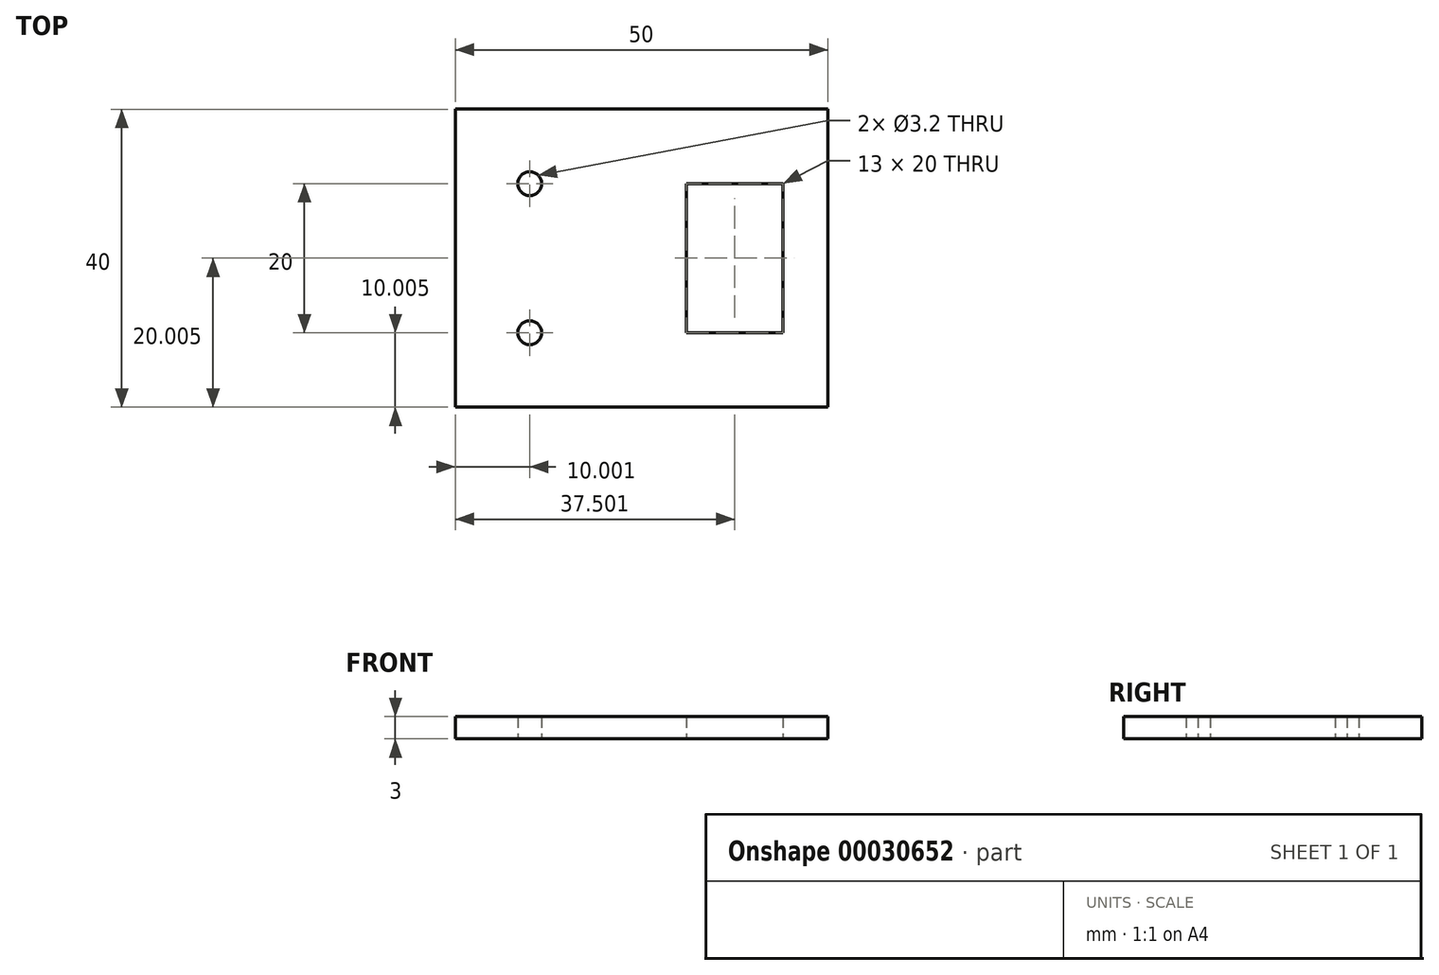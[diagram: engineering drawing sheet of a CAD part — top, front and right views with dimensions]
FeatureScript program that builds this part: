
annotation { "Feature Type Name" : "Feature", "Feature Type Description" : "" }
export const myFeature = defineFeature(function(context is Context, id is Id, definition is map)
    precondition{}
    {
        {
            var Q0;
            Q0=qCreatedBy(makeId("Top.planeOp"),FACE);
            var sketch = newSketch(context, id + "F0", { "sketchPlane" : qUnion([Q0])});
            skLineSegment(sketch, "E0.bottom", {"start": v(-26.16, 28.08) * mm, "end": v(23.84, 28.08) * mm});
            skLineSegment(sketch, "E0.top", {"start": v(-26.16, -11.92) * mm, "end": v(23.84, -11.92) * mm});
            skLineSegment(sketch, "E0.left", {"start": v(-26.16, 28.08) * mm, "end": v(-26.16, -11.92) * mm});
            skLineSegment(sketch, "E0.right", {"start": v(23.84, 28.08) * mm, "end": v(23.84, -11.92) * mm});
            skLineSegment(sketch, "E1.bottom", {"start": v(4.84, 18.08) * mm, "end": v(17.84, 18.08) * mm});
            skLineSegment(sketch, "E1.top", {"start": v(4.84, -1.92) * mm, "end": v(17.84, -1.92) * mm});
            skLineSegment(sketch, "E1.left", {"start": v(4.84, 18.08) * mm, "end": v(4.84, -1.92) * mm});
            skLineSegment(sketch, "E1.right", {"start": v(17.84, 18.08) * mm, "end": v(17.84, -1.92) * mm});
            skLineSegment(sketch, "E2", {"start": v(-26.16, 28.08) * mm, "end": v(-26.16, 18.08) * mm});
            skLineSegment(sketch, "E3", {"start": v(-26.16, 28.08) * mm, "end": v(-16.16, 28.08) * mm});
            skPoint(sketch, "E4", {"position": v(-16.16, 18.08) * mm});
            skCircle(sketch, "E5", {"center": v(-16.16, 18.08) * mm, "radius": 1.6 * mm});
            skCircle(sketch, "E6.MirrorC", {"center": v(-16.16, -1.92) * mm, "radius": 1.6 * mm});
            skSolve(sketch);
        }
        {
            var Q0;
            Q0=makeQuery(id+"F0.imprint","IMPRINT",FACE,{"disambiguationData":[TD([[makeQuery(id+"F0.imprint","IMPRINT",EDGE,{"derivedFrom":sQuery(id+"F0.wireOp",EDGE,"E0.bottom")}),-1.0]])]});
            extrude(context, id + "F1", {"entities" : qUnion([Q0]), "depth" : 3 * mm});
        }
    });
